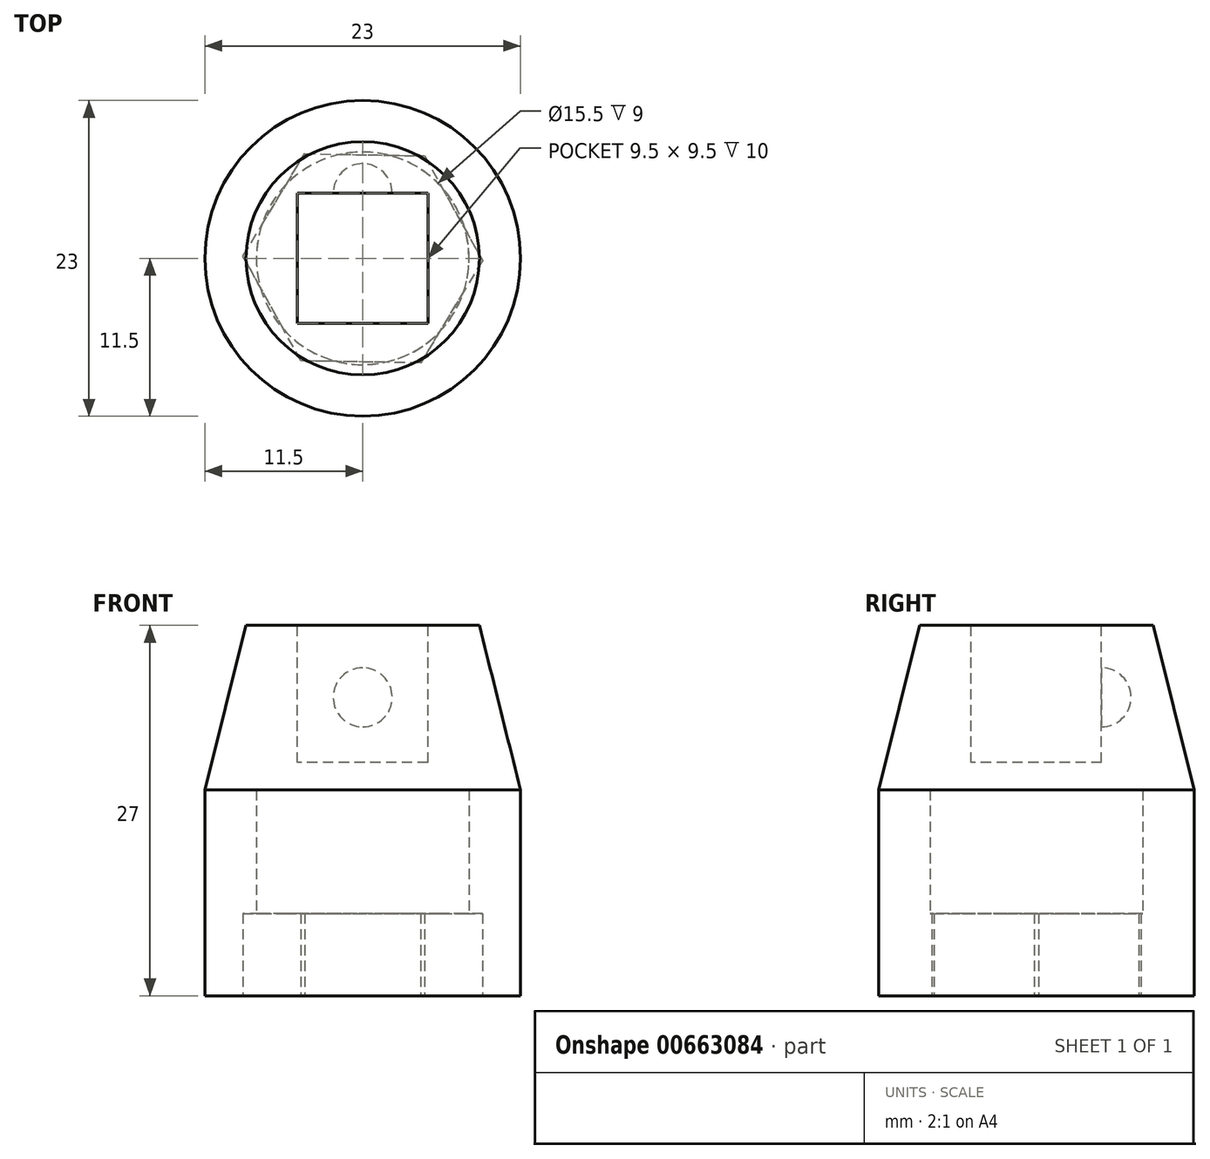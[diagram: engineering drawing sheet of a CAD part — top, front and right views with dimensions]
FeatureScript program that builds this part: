
annotation { "Feature Type Name" : "Feature", "Feature Type Description" : "" }
export const myFeature = defineFeature(function(context is Context, id is Id, definition is map)
    precondition{}
    {
        {
            var Q0;
            Q0=qCreatedBy(makeId("Top.planeOp"),FACE);
            var sketch = newSketch(context, id + "F0", { "sketchPlane" : qUnion([Q0])});
            skCircle(sketch, "E0.cCircle", {"center": v(0, 0) * mm, "radius": 7.55 * mm, "construction": true});
            skLineSegment(sketch, "E0.0", {"start": v(8.72, -0.16) * mm, "end": v(4.22, -7.63) * mm});
            skLineSegment(sketch, "E0.1", {"start": v(4.22, -7.63) * mm, "end": v(-4.5, -7.47) * mm});
            skLineSegment(sketch, "E0.2", {"start": v(-4.5, -7.47) * mm, "end": v(-8.72, 0.16) * mm});
            skLineSegment(sketch, "E0.3", {"start": v(-8.72, 0.16) * mm, "end": v(-4.22, 7.63) * mm});
            skLineSegment(sketch, "E0.4", {"start": v(-4.22, 7.63) * mm, "end": v(4.5, 7.47) * mm});
            skLineSegment(sketch, "E0.5", {"start": v(4.5, 7.47) * mm, "end": v(8.72, -0.16) * mm});
            skPoint(sketch, "E0.0.midPoint", {"position": v(6.47, -3.9) * mm});
            skCircle(sketch, "E1", {"center": v(0, 0) * mm, "radius": 11.5 * mm});
            skSolve(sketch);
        }
        {
            var Q0;
            Q0=makeQuery(id+"F0.imprint","IMPRINT",FACE,{"disambiguationData":[TD([[makeQuery(id+"F0.imprint","IMPRINT",EDGE,{"derivedFrom":sQuery(id+"F0.wireOp",EDGE,"E0.0")}),1.0]])]});
            extrude(context, id + "F1", {"entities" : qUnion([Q0]), "depth" : 6 * mm, "offsetDistance" : 25 * mm});
        }
        {
            var Q0;
            Q0=qCreatedBy(makeId("Top.planeOp"),FACE);
            cPlane(context, id + "F2", {"entities" : qUnion([Q0]), "cplaneType" : CPlaneType.OFFSET, "offset" : 6 * mm, "width" : 150 * mm, "height" : 150 * mm});
        }
        {
            var Q0;
            Q0=qCreatedBy(id+"F2.planeOp",FACE);
            var sketch = newSketch(context, id + "F3", { "sketchPlane" : qUnion([Q0])});
            skCircle(sketch, "E2", {"center": v(0, 0) * mm, "radius": 7.75 * mm});
            skCircle(sketch, "E3", {"center": v(0, 0) * mm, "radius": 11.5 * mm});
            skSolve(sketch);
        }
        {
            var Q0;
            Q0 = qSketchRegion(id + "F3", true);
            extrude(context, id + "F4", {"entities" : qUnion([Q0]), "operationType" : NewBodyOperationType.ADD, "depth" : 9 * mm, "offsetDistance" : 25 * mm});
        }
        {
            var Q0;
            Q0=makeQuery(id+"F4.opExtrude","CAP_FACE",FACE,{"disambiguationData":[OSD([sQuery(id+"F3.wireOp",EDGE,"E2"),sQuery(id+"F3.wireOp",EDGE,"E3")])],"isStart":false});
            cPlane(context, id + "F5", {"entities" : qUnion([Q0]), "cplaneType" : CPlaneType.OFFSET, "offset" : 12 * mm, "width" : 150 * mm, "height" : 150 * mm});
        }
        {
            var Q0;
            Q0=qCreatedBy(id+"F5.planeOp",FACE);
            var sketch = newSketch(context, id + "F6", { "sketchPlane" : qUnion([Q0])});
            skCircle(sketch, "E4", {"center": v(0, 0) * mm, "radius": 8.5 * mm});
            skSolve(sketch);
        }
        {
            var Q0;
            Q0=makeQuery(id+"F4.opExtrude","CAP_FACE",FACE,{"disambiguationData":[OSD([sQuery(id+"F3.wireOp",EDGE,"E2"),sQuery(id+"F3.wireOp",EDGE,"E3")])],"isStart":false});
            var sketch = newSketch(context, id + "F7", { "sketchPlane" : qUnion([Q0])});
            skCircle(sketch, "E5", {"center": v(0, 0) * mm, "radius": 11.5 * mm});
            skSolve(sketch);
        }
        {
            var Q0;
            Q0=makeQuery(id+"F6.imprint","IMPRINT",FACE,{"disambiguationData":[TD([[makeQuery(id+"F6.imprint","IMPRINT",EDGE,{"derivedFrom":sQuery(id+"F6.wireOp",EDGE,"E4")}),1.0]])]});
            var Q1;
            Q1 = qSketchRegion(id + "F7", true);
            loft(context, id + "F8", {"operationType" : NewBodyOperationType.ADD, "sheetProfilesArray" : [{ "sheetProfileEntities" : qUnion([Q0]) }, { "sheetProfileEntities" : qUnion([Q1]) }]});
        }
        {
            var Q0;
            Q0=makeQuery(id+"F6.imprint","IMPRINT",FACE,{"disambiguationData":[TD([[makeQuery(id+"F6.imprint","IMPRINT",EDGE,{"derivedFrom":sQuery(id+"F6.wireOp",EDGE,"E4")}),1.0]])]});
            var sketch = newSketch(context, id + "F9", { "sketchPlane" : qUnion([Q0])});
            skLineSegment(sketch, "E6.bottom", {"start": v(4.75, 4.75) * mm, "end": v(-4.75, 4.75) * mm});
            skLineSegment(sketch, "E6.top", {"start": v(4.75, -4.75) * mm, "end": v(-4.75, -4.75) * mm});
            skLineSegment(sketch, "E6.left", {"start": v(4.75, 4.75) * mm, "end": v(4.75, -4.75) * mm});
            skLineSegment(sketch, "E6.right", {"start": v(-4.75, 4.75) * mm, "end": v(-4.75, -4.75) * mm});
            skPoint(sketch, "E6.middle", {"position": v(0, 0) * mm});
            skSolve(sketch);
        }
        {
            var Q0;
            Q0=makeQuery(id+"F9.imprint","IMPRINT",FACE,{"disambiguationData":[TD([[makeQuery(id+"F9.imprint","IMPRINT",EDGE,{"derivedFrom":sQuery(id+"F9.wireOp",EDGE,"E6.bottom")}),1.0]])]});
            extrude(context, id + "F10", {"entities" : qUnion([Q0]), "operationType" : NewBodyOperationType.REMOVE, "oppositeDirection" : true, "depth" : 10 * mm, "offsetDistance" : 25 * mm});
        }
        {
            var Q0;
            Q0=makeQuery(id+"F10.boolean.opBoolean","COPY",FACE,{"derivedFrom":makeQuery(id+"F10.opExtrude","SWEPT_FACE",FACE,{"disambiguationData":[OSD([sQuery(id+"F9.wireOp",EDGE,"E6.bottom")])]})});
            var sketch = newSketch(context, id + "F11", { "sketchPlane" : qUnion([Q0])});
            skLineSegment(sketch, "E7", {"start": v(0, 27) * mm, "end": v(0, 21.75) * mm});
            skCircle(sketch, "E8", {"center": v(0, 21.75) * mm, "radius": 2.15 * mm});
            skLineSegment(sketch, "E9", {"start": v(0, 19.6) * mm, "end": v(0, 21.75) * mm});
            skSolve(sketch);
        }
        {
            var Q0;
            {var subQ0=sQuery(id+"F11.wireOp",EDGE,"E9");Q0=makeQuery(id+"F11.imprint","IMPRINT",FACE,{"disambiguationData":[TD([[makeQuery(id+"F11.imprint","IMPRINT",EDGE,{"derivedFrom":subQ0}),-1.0]])]});}
            var Q1;
            Q1=sQuery(id+"F11.wireOp",EDGE,"E7");
            revolve(context, id + "F12", {"operationType" : NewBodyOperationType.REMOVE, "surfaceOperationType" : NewSurfaceOperationType.NEW, "entities" : qUnion([Q0]), "axis" : qUnion([Q1]), "revolveType" : RevolveType.FULL, "oppositeDirection" : true});
        }
    });
